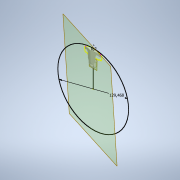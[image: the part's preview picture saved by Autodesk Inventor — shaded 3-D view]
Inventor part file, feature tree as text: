
AUTODESK INVENTOR PART (.ipt)
format: ipt  version: 2022 (Build 260153000, 153)  size: 525,824 bytes
history: native  units: mm
features: reference x14, other x11, sketch x11, extrude x9, fillet x7, projected_geometry x6, revolve x1, mirror x1
ambient origin geometry x8: Origin, YZ Plane, XZ Plane, XY Plane, X Axis, Y Axis, Z Axis, Center Point
bodies: Body1 (feature_tree)
feature tree (60):
  other  "Твердое тело1"
  extrude  "Выдавливание1"  Depth=10.6mm TaperAngle=0.0deg
  extrude  "Выдавливание2"  Depth=1.0mm
  extrude  "Выдавливание3"  Depth=1.0mm
  extrude  "Выдавливание4"  Depth=1.0mm
  extrude  "Выдавливание5"  Depth=5.5mm TaperAngle=0.0deg
  extrude  "Выдавливание6"  Depth=20.0mm TaperAngle=0.0deg
  other  "РабПлоскость2"
  extrude  "Выдавливание7"  Depth=3.0mm TaperAngle=0.0deg
  revolve  "Вращение1"
  sketch  "Эскиз10"
  other  "РабПлоскость3"
  extrude  "Выдавливание8"  Depth=4.0mm
  mirror  "Зеркальное отражение1"
  fillet  "Сопряжение2"  Radius=10.0mm
  fillet  "Сопряжение3"  Radius=7.0mm
  fillet  "Сопряжение4"  Radius=10.0mm
  fillet  "Сопряжение7"  [1 undecoded]
  fillet  "Сопряжение8"  Radius=2.5mm
  fillet  "Сопряжение9"  Radius=10.0mm
  extrude  "Выдавливание9"  TaperAngle=0.0deg  [1 undecoded]
  fillet  "Сопряжение11"  [1 undecoded]
  sketch  "Эскиз1"
  reference  "Ссылка1"
  reference  "Ссылка2"
  reference  "Ссылка3"
  reference  "Ссылка4"
  reference  "Ссылка5"
  reference  "Ссылка6"
  sketch  "Эскиз2"
  projected_geometry  "Спроецированная петля1"
  reference  "Ссылка7"
  reference  "Ссылка8"
  sketch  "Эскиз3"
  reference  "Ссылка9"
  sketch  "Эскиз4"
  projected_geometry  "Спроецированная петля2"
  sketch  "Эскиз5"
  reference  "Ссылка10"
  sketch  "Эскиз6"
  sketch  "Эскиз8"
  sketch  "Эскиз9"
  projected_geometry  "Спроецированная петля3"
  projected_geometry  "Спроецированная петля4"
  sketch  "Эскиз11"
  reference  "Ссылка11"
  reference  "Ссылка12"
  reference  "Ссылка13"
  reference  "Ссылка14"
  projected_geometry  "Спроецированная петля5"
  sketch  "Эскиз12"
  projected_geometry  "Спроецированная петля6"
  other  "<userpath>\Documents\Git\MZCAT_2024\MZCAT_2.iam"
  other  "MZCAT_2.iam"
  other  "magazine:1"
  other  "OCS-D008 B:1"
  other  "vydacha planB:1"
  other  "<userpath>\Documents\Git\MZCAT_2024\MZCAT_3.iam"
  other  "MZCAT_3.iam"
  other  "commutationCATboard:1"
note: 3 required parameter values undecoded (feature->parameter linkage not recoverable at this tier; creation-order binding heuristic only, values carry confidence <= 0.55)
